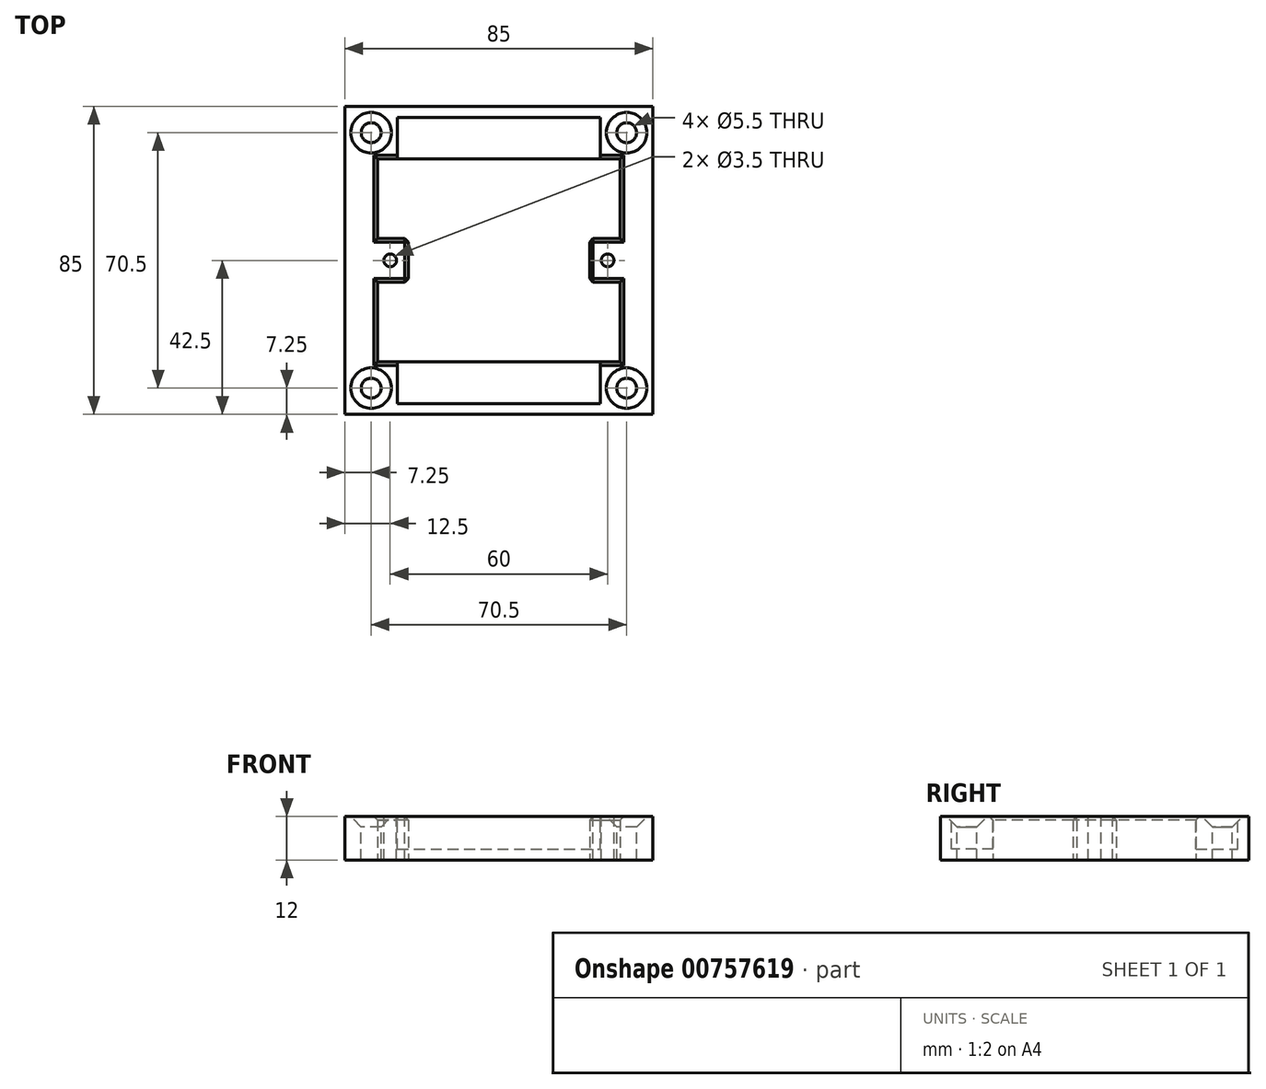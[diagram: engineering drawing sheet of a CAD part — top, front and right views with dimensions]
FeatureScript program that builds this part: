
annotation { "Feature Type Name" : "Feature", "Feature Type Description" : "" }
export const myFeature = defineFeature(function(context is Context, id is Id, definition is map)
    precondition{}
    {
        {
            var Q0;
            Q0=qCreatedBy(makeId("Top.planeOp"),FACE);
            var sketch = newSketch(context, id + "F0", { "sketchPlane" : qUnion([Q0])});
            skLineSegment(sketch, "E0.bottom", {"start": v(-42.5, -42.5) * mm, "end": v(42.5, -42.5) * mm});
            skLineSegment(sketch, "E0.top", {"start": v(-42.5, 42.5) * mm, "end": v(42.5, 42.5) * mm});
            skLineSegment(sketch, "E0.left", {"start": v(-42.5, -42.5) * mm, "end": v(-42.5, 42.5) * mm});
            skLineSegment(sketch, "E0.right", {"start": v(42.5, -42.5) * mm, "end": v(42.5, 42.5) * mm});
            skPoint(sketch, "E0.middle", {"position": v(0, 0) * mm});
            skLineSegment(sketch, "E1.bottom", {"start": v(-33.5, 28) * mm, "end": v(33.5, 28) * mm});
            skLineSegment(sketch, "E1.top", {"start": v(-33.5, -28) * mm, "end": v(33.5, -28) * mm});
            skLineSegment(sketch, "E1.left", {"start": v(-33.5, 28) * mm, "end": v(-33.5, -28) * mm});
            skLineSegment(sketch, "E1.right", {"start": v(33.5, 28) * mm, "end": v(33.5, -28) * mm});
            skLineSegment(sketch, "E2", {"start": v(-42.5, 0) * mm, "end": v(42.5, 0) * mm, "construction": true});
            skPoint(sketch, "E3", {"position": v(30, 0) * mm});
            skPoint(sketch, "E4", {"position": v(-30, 0) * mm});
            skLineSegment(sketch, "E5", {"start": v(0, 42.5) * mm, "end": v(0, -42.5) * mm, "construction": true});
            skLineSegment(sketch, "E6.bottom", {"start": v(-25, 6) * mm, "end": v(25, 6) * mm, "construction": true});
            skLineSegment(sketch, "E6.top", {"start": v(-25, -6) * mm, "end": v(25, -6) * mm, "construction": true});
            skLineSegment(sketch, "E6.left", {"start": v(-25, 6) * mm, "end": v(-25, -6) * mm, "construction": true});
            skLineSegment(sketch, "E6.right", {"start": v(25, 6) * mm, "end": v(25, -6) * mm, "construction": true});
            skLineSegment(sketch, "E7.bottom", {"start": v(-25, 6) * mm, "end": v(-42.5, 6) * mm});
            skLineSegment(sketch, "E7.top", {"start": v(-25, -6) * mm, "end": v(-42.5, -6) * mm});
            skLineSegment(sketch, "E7.left", {"start": v(-25, 6) * mm, "end": v(-25, -6) * mm});
            skLineSegment(sketch, "E7.right", {"start": v(-42.5, 6) * mm, "end": v(-42.5, -6) * mm});
            skLineSegment(sketch, "E8.bottom", {"start": v(25, -6) * mm, "end": v(42.5, -6) * mm});
            skLineSegment(sketch, "E8.top", {"start": v(25, 6) * mm, "end": v(42.5, 6) * mm});
            skLineSegment(sketch, "E8.left", {"start": v(25, -6) * mm, "end": v(25, 6) * mm});
            skLineSegment(sketch, "E8.right", {"start": v(42.5, -6) * mm, "end": v(42.5, 6) * mm});
            skLineSegment(sketch, "E9", {"start": v(-42.5, 42.5) * mm, "end": v(42.5, -42.5) * mm, "construction": true});
            skLineSegment(sketch, "E10", {"start": v(-33.5, 42.5) * mm, "end": v(-42.5, 42.5) * mm, "construction": true});
            skPoint(sketch, "E11", {"position": v(-35.25, 35.25) * mm});
            skPoint(sketch, "E12.MirrorP", {"position": v(35.25, 35.25) * mm});
            skPoint(sketch, "E13.MirrorP", {"position": v(-35.25, -35.25) * mm});
            skPoint(sketch, "E14.MirrorP", {"position": v(35.25, -35.25) * mm});
            skLineSegment(sketch, "E15", {"start": v(33.5, 28) * mm, "end": v(42.5, 28) * mm, "construction": true});
            skLineSegment(sketch, "E16", {"start": v(42.5, 28) * mm, "end": v(42.5, 42.5) * mm, "construction": true});
            skLineSegment(sketch, "E17", {"start": v(42.5, 35.25) * mm, "end": v(-42.5, 35.25) * mm, "construction": true});
            skSolve(sketch);
        }
        {
            var Q0;
            {var subQ2=sQuery(id+"F0.wireOp",EDGE,"E0.bottom");Q0=makeQuery(id+"F0.imprint","IMPRINT",FACE,{"disambiguationData":[TD([[makeQuery(id+"F0.imprint","IMPRINT",EDGE,{"derivedFrom":subQ2}),1.0]])]});}
            var Q1;
            {var subQ2=sQuery(id+"F0.wireOp",EDGE,"E0.top");Q1=makeQuery(id+"F0.imprint","IMPRINT",FACE,{"disambiguationData":[TD([[makeQuery(id+"F0.imprint","IMPRINT",EDGE,{"derivedFrom":subQ2}),-1.0]])]});}
            var Q2;
            {var subQ0=sQuery(id+"F0.wireOp",EDGE,"E7.bottom");var subQ1=sQuery(id+"F0.wireOp",EDGE,"E0.left");var subQ2=makeQuery(id+"F0.imprint","INTERSECT",VERTEX,{"derivedFrom":[subQ1,subQ0]});Q2=makeQuery(id+"F0.imprint","IMPRINT",FACE,{"disambiguationData":[TD([[makeQuery(id+"F0.imprint","IMPRINT",EDGE,{"disambiguationData":[TD([[subQ2,1.0]])],"derivedFrom":subQ1}),-1.0]])]});}
            var Q3;
            {var subQ5=sQuery(id+"F0.wireOp",EDGE,"E7.left");Q3=makeQuery(id+"F0.imprint","IMPRINT",FACE,{"disambiguationData":[TD([[makeQuery(id+"F0.imprint","IMPRINT",EDGE,{"derivedFrom":subQ5}),-1.0]])]});}
            var Q4;
            {var subQ0=sQuery(id+"F0.wireOp",EDGE,"E8.top");var subQ1=sQuery(id+"F0.wireOp",EDGE,"E0.right");var subQ2=makeQuery(id+"F0.imprint","INTERSECT",VERTEX,{"derivedFrom":[subQ1,subQ0]});Q4=makeQuery(id+"F0.imprint","IMPRINT",FACE,{"disambiguationData":[TD([[makeQuery(id+"F0.imprint","IMPRINT",EDGE,{"disambiguationData":[TD([[subQ2,1.0]])],"derivedFrom":subQ1}),1.0]])]});}
            var Q5;
            {var subQ5=sQuery(id+"F0.wireOp",EDGE,"E8.left");Q5=makeQuery(id+"F0.imprint","IMPRINT",FACE,{"disambiguationData":[TD([[makeQuery(id+"F0.imprint","IMPRINT",EDGE,{"derivedFrom":subQ5}),-1.0]])]});}
            extrude(context, id + "F1", {"entities" : qUnion([Q0, Q1, Q2, Q3, Q4, Q5]), "depth" : 12 * mm, "offsetDistance" : 25 * mm});
        }
        {
            var Q0;
            Q0=makeQuery(id+"F1.opExtrude","CAP_FACE",FACE,{"disambiguationData":[OSD([sQuery(id+"F0.wireOp",EDGE,"E0.bottom"),sQuery(id+"F0.wireOp",EDGE,"E0.top"),sQuery(id+"F0.wireOp",EDGE,"E0.left"),sQuery(id+"F0.wireOp",EDGE,"E0.right"),sQuery(id+"F0.wireOp",EDGE,"E1.bottom"),sQuery(id+"F0.wireOp",EDGE,"E1.top"),sQuery(id+"F0.wireOp",EDGE,"E1.left"),sQuery(id+"F0.wireOp",EDGE,"E1.right"),sQuery(id+"F0.wireOp",EDGE,"E7.bottom"),sQuery(id+"F0.wireOp",EDGE,"E7.top"),sQuery(id+"F0.wireOp",EDGE,"E7.left"),sQuery(id+"F0.wireOp",EDGE,"E8.bottom"),sQuery(id+"F0.wireOp",EDGE,"E8.top"),sQuery(id+"F0.wireOp",EDGE,"E8.left")])],"isStart":false});
            var sketch = newSketch(context, id + "F2", { "sketchPlane" : qUnion([Q0])});
            skPoint(sketch, "E18.0", {"position": v(30, 0) * mm});
            skPoint(sketch, "E18.1", {"position": v(-30, 0) * mm});
            skPoint(sketch, "E19.0", {"position": v(-35.25, 35.25) * mm});
            skPoint(sketch, "E19.1", {"position": v(-35.25, -35.25) * mm});
            skPoint(sketch, "E19.2", {"position": v(35.25, 35.25) * mm});
            skPoint(sketch, "E19.3", {"position": v(35.25, -35.25) * mm});
            skSolve(sketch);
        }
        {
            var Q0;
            Q0=sQuery(id+"F2.wireOp",VERTEX,"E18.1");
            var Q1;
            Q1=sQuery(id+"F2.wireOp",VERTEX,"E18.0");
            var Q2;
            Q2=makeQuery(id+"F1.opExtrude","SWEPT_BODY",BODY,{"disambiguationData":[OSD([sQuery(id+"F0.wireOp",EDGE,"E0.bottom"),sQuery(id+"F0.wireOp",EDGE,"E0.top"),sQuery(id+"F0.wireOp",EDGE,"E0.left"),sQuery(id+"F0.wireOp",EDGE,"E0.right"),sQuery(id+"F0.wireOp",EDGE,"E1.bottom"),sQuery(id+"F0.wireOp",EDGE,"E1.top"),sQuery(id+"F0.wireOp",EDGE,"E1.left"),sQuery(id+"F0.wireOp",EDGE,"E1.right"),sQuery(id+"F0.wireOp",EDGE,"E7.bottom"),sQuery(id+"F0.wireOp",EDGE,"E7.top"),sQuery(id+"F0.wireOp",EDGE,"E7.left"),sQuery(id+"F0.wireOp",EDGE,"E8.bottom"),sQuery(id+"F0.wireOp",EDGE,"E8.top"),sQuery(id+"F0.wireOp",EDGE,"E8.left")])]});
            hole(context, id + "F3", {"style" : HoleStyle.SIMPLE, "endStyle" : HoleEndStyle.THROUGH, "standardTappedOrClearance" : lookupTablePath({ "standard" : "ISO", "size" : "3.5", "type" : "Drilled" }), "standardBlindInLast" : lookupTablePath({ "standard" : "ISO", "size" : "3.5", "type" : "Drilled" }), "holeDiameter" : 3.5 * mm, "majorDiameter" : 5 * mm, "isTappedThrough" : true, "tappedDepth" : 12 * mm, "tapClearance" : 3, "startFromSketch" : true, "locations" : qUnion([Q0, Q1]), "scope" : qUnion([Q2])});
        }
        {
            var Q0;
            Q0=sQuery(id+"F2.wireOp",VERTEX,"E19.0");
            var Q1;
            Q1=sQuery(id+"F2.wireOp",VERTEX,"E19.2");
            var Q2;
            Q2=sQuery(id+"F2.wireOp",VERTEX,"E19.3");
            var Q3;
            Q3=sQuery(id+"F2.wireOp",VERTEX,"E19.1");
            var Q4;
            Q4=makeQuery(id+"F1.opExtrude","SWEPT_BODY",BODY,{"disambiguationData":[OSD([sQuery(id+"F0.wireOp",EDGE,"E0.bottom"),sQuery(id+"F0.wireOp",EDGE,"E0.top"),sQuery(id+"F0.wireOp",EDGE,"E0.left"),sQuery(id+"F0.wireOp",EDGE,"E0.right"),sQuery(id+"F0.wireOp",EDGE,"E1.bottom"),sQuery(id+"F0.wireOp",EDGE,"E1.top"),sQuery(id+"F0.wireOp",EDGE,"E1.left"),sQuery(id+"F0.wireOp",EDGE,"E1.right"),sQuery(id+"F0.wireOp",EDGE,"E7.bottom"),sQuery(id+"F0.wireOp",EDGE,"E7.top"),sQuery(id+"F0.wireOp",EDGE,"E7.left"),sQuery(id+"F0.wireOp",EDGE,"E8.bottom"),sQuery(id+"F0.wireOp",EDGE,"E8.top"),sQuery(id+"F0.wireOp",EDGE,"E8.left")])]});
            hole(context, id + "F4", {"style" : HoleStyle.C_SINK, "endStyle" : HoleEndStyle.THROUGH, "standardTappedOrClearance" : lookupTablePath({ "standard" : "ISO", "fit" : "Normal", "size" : "M5", "type" : "Clearance" }), "standardBlindInLast" : lookupTablePath({ "fit" : "Standard", "standard" : "ISO", "size" : "M5", "type" : "Clearance" }), "holeDiameter" : 5.5 * mm, "cSinkDiameter" : 11.2 * mm, "cSinkAngle" : 90 * degree, "majorDiameter" : 5 * mm, "isTappedThrough" : true, "tappedDepth" : 12 * mm, "tapClearance" : 3, "locations" : qUnion([Q0, Q1, Q2, Q3]), "scope" : qUnion([Q4])});
        }
        {
            var Q0;
            Q0=makeQuery(id+"F2.imprint","IMPRINT",FACE,{"disambiguationData":[TD([[makeQuery(id+"F2.imprint","IMPRINT",EDGE,{"derivedFrom":makeQuery(id+"F1.opExtrude","CAP_EDGE",EDGE,{"disambiguationData":[OSD([sQuery(id+"F0.wireOp",EDGE,"E0.bottom")])],"isStart":false})}),1.0]])]});
            var sketch = newSketch(context, id + "F5", { "sketchPlane" : qUnion([Q0])});
            skLineSegment(sketch, "E20.bottom", {"start": v(28, 28) * mm, "end": v(-28, 28) * mm});
            skLineSegment(sketch, "E20.top", {"start": v(28, 39.5) * mm, "end": v(-28, 39.5) * mm});
            skLineSegment(sketch, "E20.left", {"start": v(28, 28) * mm, "end": v(28, 39.5) * mm});
            skLineSegment(sketch, "E20.right", {"start": v(-28, 28) * mm, "end": v(-28, 39.5) * mm});
            skPoint(sketch, "E20.middle", {"position": v(0, 33.75) * mm});
            skLineSegment(sketch, "E21", {"start": v(-53.37, 0) * mm, "end": v(59.54, 0) * mm, "construction": true});
            skLineSegment(sketch, "E22.MirrorCS", {"start": v(28, -28) * mm, "end": v(-28, -28) * mm});
            skLineSegment(sketch, "E23.MirrorCS", {"start": v(28, -39.5) * mm, "end": v(-28, -39.5) * mm});
            skLineSegment(sketch, "E24.MirrorCS", {"start": v(28, -28) * mm, "end": v(28, -39.5) * mm});
            skLineSegment(sketch, "E25.MirrorCS", {"start": v(-28, -28) * mm, "end": v(-28, -39.5) * mm});
            skSolve(sketch);
        }
        {
            var Q0;
            Q0=makeQuery(id+"F5.imprint","IMPRINT",FACE,{"disambiguationData":[TD([[makeQuery(id+"F5.imprint","IMPRINT",EDGE,{"derivedFrom":sQuery(id+"F5.wireOp",EDGE,"E22.MirrorCS")}),-1.0]])]});
            var Q1;
            Q1=makeQuery(id+"F5.imprint","IMPRINT",FACE,{"disambiguationData":[TD([[makeQuery(id+"F5.imprint","IMPRINT",EDGE,{"derivedFrom":sQuery(id+"F5.wireOp",EDGE,"E20.bottom")}),1.0]])]});
            extrude(context, id + "F6", {"entities" : qUnion([Q0, Q1]), "operationType" : NewBodyOperationType.REMOVE, "oppositeDirection" : true, "depth" : 9 * mm, "offsetDistance" : 25 * mm});
        }
        {
            var Q0;
            {var subQ2=sQuery(id+"F0.wireOp",EDGE,"E1.bottom");Q0=makeQuery(id+"F6.boolean.opBoolean","SPLIT",EDGE,{"disambiguationData":[TD([makeQuery(id+"F6.opExtrude","SWEPT_FACE",FACE,{"disambiguationData":[OSD([sQuery(id+"F5.wireOp",EDGE,"E20.right")])]})])],"derivedFrom":makeQuery(id+"F1.opExtrude","CAP_EDGE",EDGE,{"disambiguationData":[OSD([subQ2])],"isStart":false})});}
            var Q1;
            {var subQ0=sQuery(id+"F0.wireOp",EDGE,"E1.left");Q1=makeQuery(id+"F1.opExtrude","CAP_EDGE",EDGE,{"disambiguationData":[OSD([subQ0]),TDD([makeQuery(id+"F0.imprint","IMPRINT",EDGE,{"disambiguationData":[TD([[makeQuery(id+"F0.imprint","INTERSECT",VERTEX,{"derivedFrom":[sQuery(id+"F0.wireOp",EDGE,"E1.bottom"),subQ0]}),-1.0]])],"derivedFrom":subQ0})])],"isStart":false});}
            var Q2;
            Q2=makeQuery(id+"F1.opExtrude","CAP_EDGE",EDGE,{"disambiguationData":[OSD([sQuery(id+"F0.wireOp",EDGE,"E7.bottom")])],"isStart":false});
            var Q3;
            Q3=makeQuery(id+"F1.opExtrude","CAP_EDGE",EDGE,{"disambiguationData":[OSD([sQuery(id+"F0.wireOp",EDGE,"E7.left")])],"isStart":false});
            var Q4;
            Q4=makeQuery(id+"F1.opExtrude","CAP_EDGE",EDGE,{"disambiguationData":[OSD([sQuery(id+"F0.wireOp",EDGE,"E7.top")])],"isStart":false});
            var Q5;
            {var subQ0=sQuery(id+"F0.wireOp",EDGE,"E1.left");Q5=makeQuery(id+"F1.opExtrude","CAP_EDGE",EDGE,{"disambiguationData":[OSD([subQ0]),TDD([makeQuery(id+"F0.imprint","IMPRINT",EDGE,{"disambiguationData":[TD([[makeQuery(id+"F0.imprint","INTERSECT",VERTEX,{"derivedFrom":[sQuery(id+"F0.wireOp",EDGE,"E1.top"),subQ0]}),1.0]])],"derivedFrom":subQ0})])],"isStart":false});}
            var Q6;
            {var subQ2=sQuery(id+"F0.wireOp",EDGE,"E1.top");Q6=makeQuery(id+"F6.boolean.opBoolean","SPLIT",EDGE,{"disambiguationData":[TD([makeQuery(id+"F6.opExtrude","SWEPT_FACE",FACE,{"disambiguationData":[OSD([sQuery(id+"F5.wireOp",EDGE,"E25.MirrorCS")])]})])],"derivedFrom":makeQuery(id+"F1.opExtrude","CAP_EDGE",EDGE,{"disambiguationData":[OSD([subQ2])],"isStart":false})});}
            var Q7;
            {var subQ2=sQuery(id+"F0.wireOp",EDGE,"E1.bottom");Q7=makeQuery(id+"F6.boolean.opBoolean","SPLIT",EDGE,{"disambiguationData":[TD([makeQuery(id+"F6.opExtrude","SWEPT_FACE",FACE,{"disambiguationData":[OSD([sQuery(id+"F5.wireOp",EDGE,"E20.left")])]})])],"derivedFrom":makeQuery(id+"F1.opExtrude","CAP_EDGE",EDGE,{"disambiguationData":[OSD([subQ2])],"isStart":false})});}
            var Q8;
            {var subQ0=sQuery(id+"F0.wireOp",EDGE,"E1.right");Q8=makeQuery(id+"F1.opExtrude","CAP_EDGE",EDGE,{"disambiguationData":[OSD([subQ0]),TDD([makeQuery(id+"F0.imprint","IMPRINT",EDGE,{"disambiguationData":[TD([[makeQuery(id+"F0.imprint","INTERSECT",VERTEX,{"derivedFrom":[sQuery(id+"F0.wireOp",EDGE,"E1.bottom"),subQ0]}),-1.0]])],"derivedFrom":subQ0})])],"isStart":false});}
            var Q9;
            Q9=makeQuery(id+"F1.opExtrude","CAP_EDGE",EDGE,{"disambiguationData":[OSD([sQuery(id+"F0.wireOp",EDGE,"E8.top")])],"isStart":false});
            var Q10;
            Q10=makeQuery(id+"F1.opExtrude","CAP_EDGE",EDGE,{"disambiguationData":[OSD([sQuery(id+"F0.wireOp",EDGE,"E8.left")])],"isStart":false});
            var Q11;
            Q11=makeQuery(id+"F1.opExtrude","CAP_EDGE",EDGE,{"disambiguationData":[OSD([sQuery(id+"F0.wireOp",EDGE,"E8.bottom")])],"isStart":false});
            var Q12;
            {var subQ0=sQuery(id+"F0.wireOp",EDGE,"E1.right");Q12=makeQuery(id+"F1.opExtrude","CAP_EDGE",EDGE,{"disambiguationData":[OSD([subQ0]),TDD([makeQuery(id+"F0.imprint","IMPRINT",EDGE,{"disambiguationData":[TD([[makeQuery(id+"F0.imprint","INTERSECT",VERTEX,{"derivedFrom":[sQuery(id+"F0.wireOp",EDGE,"E1.top"),subQ0]}),1.0]])],"derivedFrom":subQ0})])],"isStart":false});}
            var Q13;
            {var subQ2=sQuery(id+"F0.wireOp",EDGE,"E1.top");Q13=makeQuery(id+"F6.boolean.opBoolean","SPLIT",EDGE,{"disambiguationData":[TD([makeQuery(id+"F6.opExtrude","SWEPT_FACE",FACE,{"disambiguationData":[OSD([sQuery(id+"F5.wireOp",EDGE,"E24.MirrorCS")])]})])],"derivedFrom":makeQuery(id+"F1.opExtrude","CAP_EDGE",EDGE,{"disambiguationData":[OSD([subQ2])],"isStart":false})});}
            var Q14;
            Q14=makeQuery(id+"F6.boolean.opBoolean","COPY",EDGE,{"derivedFrom":makeQuery(id+"F6.opExtrude","SWEPT_EDGE",EDGE,{"disambiguationData":[OSD([sQuery(id+"F0.wireOp",EDGE,"E1.top"),sQuery(id+"F5.wireOp",EDGE,"E22.MirrorCS"),sQuery(id+"F5.wireOp",EDGE,"E25.MirrorCS")])]})});
            var Q15;
            Q15=makeQuery(id+"F6.boolean.opBoolean","COPY",EDGE,{"derivedFrom":makeQuery(id+"F6.opExtrude","SWEPT_EDGE",EDGE,{"disambiguationData":[OSD([sQuery(id+"F0.wireOp",EDGE,"E1.top"),sQuery(id+"F5.wireOp",EDGE,"E22.MirrorCS"),sQuery(id+"F5.wireOp",EDGE,"E24.MirrorCS")])]})});
            var Q16;
            Q16=makeQuery(id+"F6.boolean.opBoolean","COPY",EDGE,{"derivedFrom":makeQuery(id+"F6.opExtrude","SWEPT_EDGE",EDGE,{"disambiguationData":[OSD([sQuery(id+"F0.wireOp",EDGE,"E1.bottom"),sQuery(id+"F5.wireOp",EDGE,"E20.bottom"),sQuery(id+"F5.wireOp",EDGE,"E20.right")])]})});
            var Q17;
            Q17=makeQuery(id+"F6.boolean.opBoolean","COPY",EDGE,{"derivedFrom":makeQuery(id+"F6.opExtrude","SWEPT_EDGE",EDGE,{"disambiguationData":[OSD([sQuery(id+"F0.wireOp",EDGE,"E1.bottom"),sQuery(id+"F5.wireOp",EDGE,"E20.bottom"),sQuery(id+"F5.wireOp",EDGE,"E20.left")])]})});
            var Q18;
            Q18=makeQuery(id+"F1.opExtrude","SWEPT_EDGE",EDGE,{"disambiguationData":[OSD([sQuery(id+"F0.wireOp",EDGE,"E7.bottom"),sQuery(id+"F0.wireOp",EDGE,"E7.left")])]});
            var Q19;
            Q19=makeQuery(id+"F1.opExtrude","SWEPT_EDGE",EDGE,{"disambiguationData":[OSD([sQuery(id+"F0.wireOp",EDGE,"E7.top"),sQuery(id+"F0.wireOp",EDGE,"E7.left")])]});
            var Q20;
            Q20=makeQuery(id+"F1.opExtrude","SWEPT_EDGE",EDGE,{"disambiguationData":[OSD([sQuery(id+"F0.wireOp",EDGE,"E8.top"),sQuery(id+"F0.wireOp",EDGE,"E8.left")])]});
            var Q21;
            Q21=makeQuery(id+"F1.opExtrude","SWEPT_EDGE",EDGE,{"disambiguationData":[OSD([sQuery(id+"F0.wireOp",EDGE,"E8.bottom"),sQuery(id+"F0.wireOp",EDGE,"E8.left")])]});
            var Q22;
            Q22=makeQuery(id+"F6.boolean.opBoolean","COPY",EDGE,{"derivedFrom":makeQuery(id+"F6.opExtrude","CAP_EDGE",EDGE,{"disambiguationData":[OSD([sQuery(id+"F5.wireOp",EDGE,"E20.right")])],"isStart":true})});
            var Q23;
            Q23=makeQuery(id+"F6.boolean.opBoolean","COPY",EDGE,{"derivedFrom":makeQuery(id+"F6.opExtrude","CAP_EDGE",EDGE,{"disambiguationData":[OSD([sQuery(id+"F5.wireOp",EDGE,"E20.left")])],"isStart":true})});
            var Q24;
            Q24=makeQuery(id+"F6.boolean.opBoolean","COPY",EDGE,{"derivedFrom":makeQuery(id+"F6.opExtrude","CAP_EDGE",EDGE,{"disambiguationData":[OSD([sQuery(id+"F5.wireOp",EDGE,"E24.MirrorCS")])],"isStart":true})});
            var Q25;
            Q25=makeQuery(id+"F6.boolean.opBoolean","COPY",EDGE,{"derivedFrom":makeQuery(id+"F6.opExtrude","CAP_EDGE",EDGE,{"disambiguationData":[OSD([sQuery(id+"F5.wireOp",EDGE,"E25.MirrorCS")])],"isStart":true})});
            chamfer(context, id + "F7", {"entities" : qUnion([Q0, Q1, Q2, Q3, Q4, Q5, Q6, Q7, Q8, Q9, Q10, Q11, Q12, Q13, Q14, Q15, Q16, Q17, Q18, Q19, Q20, Q21, Q22, Q23, Q24, Q25]), "width" : 1 * mm, "tangentPropagation" : true});
        }
    });
